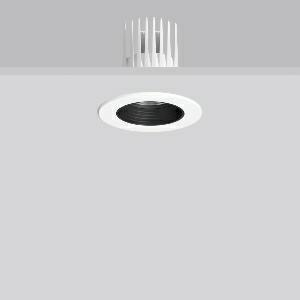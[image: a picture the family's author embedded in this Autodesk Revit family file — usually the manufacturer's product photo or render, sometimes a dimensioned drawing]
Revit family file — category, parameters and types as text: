
# Revit family: heledon_mini_e_901754_002_2bbd
name_source: partatom
category: Lighting Fixtures
units: mm (PartAtom-declared; Revit-internal decimal feet)

## family parameters
Cut with Voids When Loaded = No
Host = Face
Light Source = No
Part Type = Normal
Room Calculation Point = No
Round Connector Dimension = Use Diameter
Shared = No

## types (1)
- HELEDON mini E (1 x LED Modul 930, 3250 lm, 3000)
    Apparent Load = 29 VA
    Approval mark = CE
    CIE Flux Codes = 80 99 100 100 100
    Color Rendering = 90
    Color Temperature = 3000
    Default Elevation = 1800 mm
    Description = Series: HELEDON mini
Round recessed downlight. Housing: die-cast aluminium, powder-coated. Black plastic ring and recessed LED to prevent glare from the side. Optical assembly with lens made of plastic (polycarbonate) for the best homogeneous light distribution - can be changed without tools. Best colour rendering index Ra>90. Suitable for Recessed ceiling mounting. Installation without tools thanks to spring fastening system. Including separate LED converter with connecting cable 600 mm.High quality converter without flickering and stroboscopic effect. Through-wiring box (5 pole) available as accessory. The following accessories can be mounted without use of tools: interchangeable lenses, decorative glasses, honeycomb louvre, clear and frosted diffusers, white interchangeable plastic ring. 
Colour: traffic white, matt (RAL 9016)
Diameter: 124 mm
Height: 3 mm
Cut-out diameter: 114 mm
Recess height: 170 mm
Luminaire: recess height: 120 mm
Lamp: LED
Socket: without socket
Colour temperature: 3000K
Colour rendering index (CRI): 92
System power: 29 W
Rated luminous flux: 3250 lm
Luminous efficiency: 112 lm/W
Control gear: Regulated power supply
Protection class: II
Type of protection: IP 20
    Height = 0 mm  [stored 0 ft]
    Lamp = 1 x LED Modul 930
    Lamp Light Flux = 3250 lm
    Lamp count = 1
    Length = 124 mm  [stored 0.406824 ft]
    Lifetime = 50000 h
    Luminous efficacy = 112 lm/W
    Manufacturer = RZB
    ModVariant = No
    Model = 901754.002
    Mounting Place = Ceiling
    Mounting Type = Recessed
    Number of Poles = 1
    OnlyDefault = Yes
    Power Factor = 1
    Product Name = HELEDON mini E
    Product group = Recessed downlights
    ProductGroupID = 402
    Protection Class = Protection class II
    Protection Degree = IP 20
    RLX_Detail_Level = 1
    RLX_Emergency_Light_Flux = 0 lm
    RLX_Emergency_Type = 0
    RLX_Emergency_Type_DB = No
    RlxData = <blob elided: 126717 chars, md5=0a3ef809>
    Socket = socket
    Standby Power = 0 W
    System Light Flux = 3250 lm
    System Power = 29 W
    Type Comments = Product without accessories
    Type Image = 901656.002.jpg
    URL = http://relux.com
    VarID = ---
    Voltage = 230 V
    Voltage Range = 220-240 V
    Weight = 0.00 kg
    Width = 0 mm  [stored 0 ft]

note: [stored X ft] marks values corroborated as IEEE doubles in the binary element streams (Revit-internal decimal feet)

## geometry (parser evidence)
native form markers: Blend x4, Sweep x11
no freeform markers — native parametric forms only
